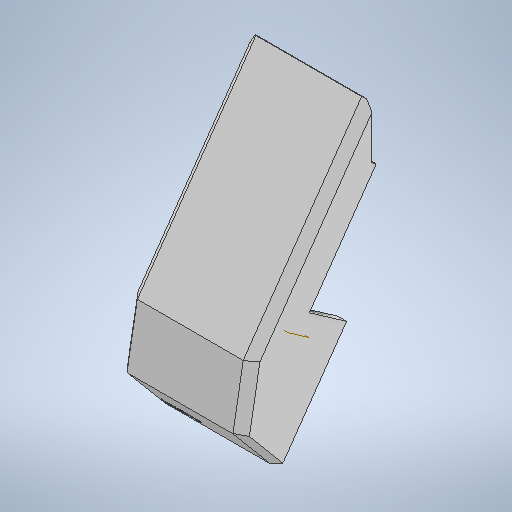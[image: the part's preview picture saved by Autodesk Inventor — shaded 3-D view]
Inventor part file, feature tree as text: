
AUTODESK INVENTOR PART (.ipt)
format: ipt  version: 2025.2 (Build 292293000, 293)  size: 1,496,064 bytes
history: native  units: in
note: dims shown in document units (in); Inventor stores cm internally (conversion verified against a paired STEP export)
features: sketch x48, extrude x43, projected_geometry x14, plane x10, move_body x1, chamfer x1, fillet x1, thicken_offset x1, hole x1
ambient origin geometry x8: Origin, YZ Plane, XZ Plane, XY Plane, X Axis, Y Axis, Z Axis, Center Point
bodies: Solid1 (feature_tree)
feature tree (120):
  extrude  "Extrusion1"  Depth=0.1969in TaperAngle=0.0deg
  move_body  "Move Body1"
  plane  "Work Plane1"
  sketch  "Sketch5"  dims[d5=1.7717in d6=1.7717in d7=1.7717in d8=1.7717in d9=0.8108in d10=90.0deg d11=0.0787in d12=0.3701in d13=0.4252in d14=0.1362in d15=-0.0984in d16=-0.0591in d17=0.0in]
  plane  "Work Plane2"
  extrude  "Extrusion4"  TaperAngle=0.0deg  [1 undecoded]
  extrude  "Extrusion6"  Depth=0.2405in
  extrude  "Extrusion8"  Depth=2.5591in TaperAngle=0.0deg
  chamfer  "Chamfer1"  [1 undecoded]
  extrude  "Extrusion11"  Depth=0.2362in
  plane  "Work Plane3"
  plane  "Work Plane7"
  extrude  "Extrusion22"  Depth=0.0787in TaperAngle=0.0deg
  extrude  "Extrusion25"  Depth=0.5027in
  extrude  "Extrusion26"  Depth=0.5027in
  sketch  "Sketch33"  dims[d96=0.2362in d97=0.0in d100=3.6403in]
  extrude  "Extrusion27"  Depth=0.2362in TaperAngle=0.0deg
  extrude  "Extrusion28"  Depth=3.6403in
  sketch  "Sketch36"  dims[d123=0.9331in d124=0.9712in d125=0.0in]
  extrude  "Extrusion29"  Depth=1.9685in
  extrude  "Extrusion30"  Depth=0.1575in
  extrude  "Extrusion31"  Depth=0.9712in TaperAngle=0.0deg
  sketch  "Sketch39"  dims[d138=0.4331in d139=0.1181in d140=0.0in]
  extrude  "Extrusion32"  Depth=11.3469in TaperAngle=0.0deg
  fillet  "Fillet1"  Radius=11.3469in
  extrude  "Extrusion33"  Depth=0.4331in
  extrude  "Extrusion34"  Depth=0.1181in TaperAngle=0.0deg
  extrude  "Extrusion35"  Depth=0.0787in
  plane  "Work Plane8"
  sketch  "Sketch45"  dims[d160=0.1181in d161=0.0in d162=0.1969in d163=0.0in d164=0.1181in d165=0.0in]
  extrude  "Extrusion37"  Depth=0.2756in
  extrude  "Extrusion38"  Depth=0.1181in TaperAngle=0.0deg
  extrude  "Extrusion40"  Depth=0.5906in
  extrude  "Extrusion41"  Depth=0.1181in TaperAngle=0.0deg
  extrude  "Extrusion43"  Depth=4.7244in TaperAngle=0.0deg
  extrude  "Extrusion44"  Depth=0.7313in TaperAngle=0.0deg
  extrude  "Extrusion46"  TaperAngle=0.0deg  [1 undecoded]
  extrude  "Extrusion48"  Depth=1.1024in
  extrude  "Extrusion50"  Depth=0.0394in TaperAngle=0.0deg
  extrude  "Extrusion51"  Depth=5.8937in TaperAngle=0.0deg
  extrude  "Extrusion53"  Depth=2.3622in TaperAngle=0.0deg
  plane  "Work Plane9"
  plane  "Work Plane12"
  extrude  "Extrusion65"  Depth=0.1969in
  plane  "Work Plane13"
  extrude  "Extrusion67"  TaperAngle=60.0deg  [1 undecoded]
  plane  "Work Plane14"
  extrude  "Extrusion68"  Depth=0.7902in
  extrude  "Extrusion69"  Depth=0.3436in
  extrude  "Extrusion70"  Depth=0.2362in
  sketch  "Sketch84"  dims[d298=0.2362in d299=0.0in d300=0.2362in d301=0.0in]
  extrude  "Extrusion71"  TaperAngle=0.0deg  [1 undecoded]
  extrude  "Extrusion72"  Depth=0.2362in TaperAngle=0.0deg
  extrude  "Extrusion73"  TaperAngle=90.0deg  [1 undecoded]
  extrude  "Extrusion74"  Depth=0.2362in TaperAngle=0.0deg
  extrude  "Extrusion75"  TaperAngle=0.0deg  [1 undecoded]
  extrude  "Extrusion76"  Depth=0.0787in
  thicken_offset  "Thicken1"
  extrude  "Extrusion78"  TaperAngle=90.0deg  [1 undecoded]
  plane  "Work Plane15"
  extrude  "Extrusion79"  Depth=0.0787in
  extrude  "Extrusion80"  Depth=0.0787in TaperAngle=0.0deg
  extrude  "Extrusion81"  TaperAngle=0.0deg  [1 undecoded]
  sketch  "Sketch1"  dims[d1=0.5512in d2=0.1969in d3=0.0in]
  sketch  "Sketch6"  dims[d18=0.2749in d24=0.2405in]
  sketch  "Sketch8"  dims[d25=2.7559in d26=0.0in d29=2.5591in d30=0.0in d36=0.0in d37=0.0in]
  sketch  "Sketch12"  dims[d42=0.2362in d43=0.2362in]
  sketch  "Sketch15"  dims[d52=0.2362in d53=0.0787in d54=45.0deg d55=0.1969in d56=0.0in]
  sketch  "Sketch28"  dims[d76=0.5027in d77=0.5027in]
  sketch  "Sketch31"  dims[d78=0.5027in d79=0.5027in]
  sketch  "Sketch32"  dims[d83=0.0in d84=0.0in d94=0.2362in d95=0.0in]
  sketch  "Sketch34"  dims[d101=2.7717in d112=1.9685in]
  sketch  "Sketch35"  dims[d113=0.6299in d114=0.0in d115=0.1575in d117=0.1575in d121=1.9685in d122=0.7874in]
  sketch  "Sketch37"  dims[d126=0.5906in d127=0.0in d128=11.3469in d129=0.0in d130=11.3469in d131=0.0in]
  sketch  "Sketch38"  dims[d136=0.4331in d137=0.4331in]
  sketch  "Sketch40"  dims[d141=0.6299in d142=0.0787in]
  sketch  "Sketch41"  dims[d147=0.2756in d149=0.2756in]
  sketch  "Sketch42"  dims[d150=0.0in d151=0.0in d154=0.1181in d155=0.0in]
  sketch  "Sketch44"  dims[d156=0.1181in d157=0.0in d158=0.5906in]
  projected_geometry  "Projected Loop2"
  projected_geometry  "Projected Loop3"
  projected_geometry  "Projected Loop5"
  sketch  "Sketch47"  dims[d168=0.5906in d169=0.0in d170=4.7244in d171=0.0in]
  sketch  "Sketch49"  dims[d174=0.0in d175=0.0in d176=0.7313in d177=0.0in]
  sketch  "Sketch50"  dims[d186=0.0in d187=0.0in d188=0.0in d189=0.0in]
  sketch  "Sketch52"  dims[d194=0.0in d195=0.0in d196=1.1024in]
  sketch  "Sketch53"  dims[d197=0.5906in d200=0.0394in d201=0.0in]
  sketch  "Sketch56"  dims[d218=0.0in d219=0.0in d220=5.8937in d221=0.0in]
  sketch  "Sketch59"  dims[d233=0.9963in d234=2.3622in d235=0.0in]
  sketch  "Sketch60"  dims[d266=0.1378in d268=0.1969in]
  sketch  "Sketch61"  dims[d269=0.1378in d270=60.0deg]
  sketch  "Sketch63"  dims[d271=4.5565in d272=0.0in d277=0.7902in]
  projected_geometry  "Projected Loop8"
  sketch  "Sketch76"  dims[d278=0.5906in d279=1.378in d280=0.0in d281=0.0in d282=0.3436in]
  sketch  "Sketch78"  dims[d283=1.378in d284=0.9843in d285=0.0in d286=0.0in d287=0.2362in]
  projected_geometry  "Projected Loop14"
  sketch  "Sketch79"  dims[d288=0.0in d289=0.0in d290=0.0in d291=0.0in]
  projected_geometry  "Projected Loop15"
  projected_geometry  "Projected Loop16"
  projected_geometry  "Projected Loop17"
  sketch  "Sketch80"  dims[d292=0.5894in d293=0.2362in d294=0.0in]
  projected_geometry  "Projected Loop18"
  projected_geometry  "Projected Loop20"
  sketch  "Sketch83"  dims[d295=0.2362in d296=0.0in d297=90.0deg]
  projected_geometry  "Projected Loop22"
  sketch  "Sketch85"  dims[d302=0.0787in d303=0.0in d304=0.0in d305=0.0in]
  sketch  "Sketch86"  dims[d306=0.0787in d307=0.0787in]
  sketch  "Sketch87"  dims[d314=0.1181in d315=0.0in d316=90.0deg]
  sketch  "Sketch88"  dims[d317=0.0787in d318=0.0787in]
  sketch  "Sketch89"  dims[d319=0.0787in d320=1.7037in d321=0.0in]
  sketch  "Sketch90"  dims[d322=0.0787in d323=0.0in d324=0.0in]
  projected_geometry  "Projected Loop23"
  sketch  "Sketch92"  dims[d325=0.0in d326=0.0in d38=0.0197in]
  projected_geometry  "Projected Loop25"
  projected_geometry  "Projected Loop26"
  sketch  "Sketch94"  dims[d39=0.0344in]
  sketch  "Sketch95"  dims[d57=0.0197in]
  sketch  "Sketch96"  dims[d58=0.0344in d59=0.0197in d60=0.0344in d81=0.0197in d82=0.0344in d159=0.0344in d178=0.0in d179=0.0in d180=0.0in d181=0.0in d202=0.0197in d203=0.0344in d222=0.0197in d223=0.0344in]
  sketch  "Sketch2"  dims[d4=0.315in]
  hole  "Hole1"  [1 undecoded]
note: 10 required parameter values undecoded (feature->parameter linkage not recoverable at this tier; creation-order binding heuristic only, values carry confidence <= 0.55)
